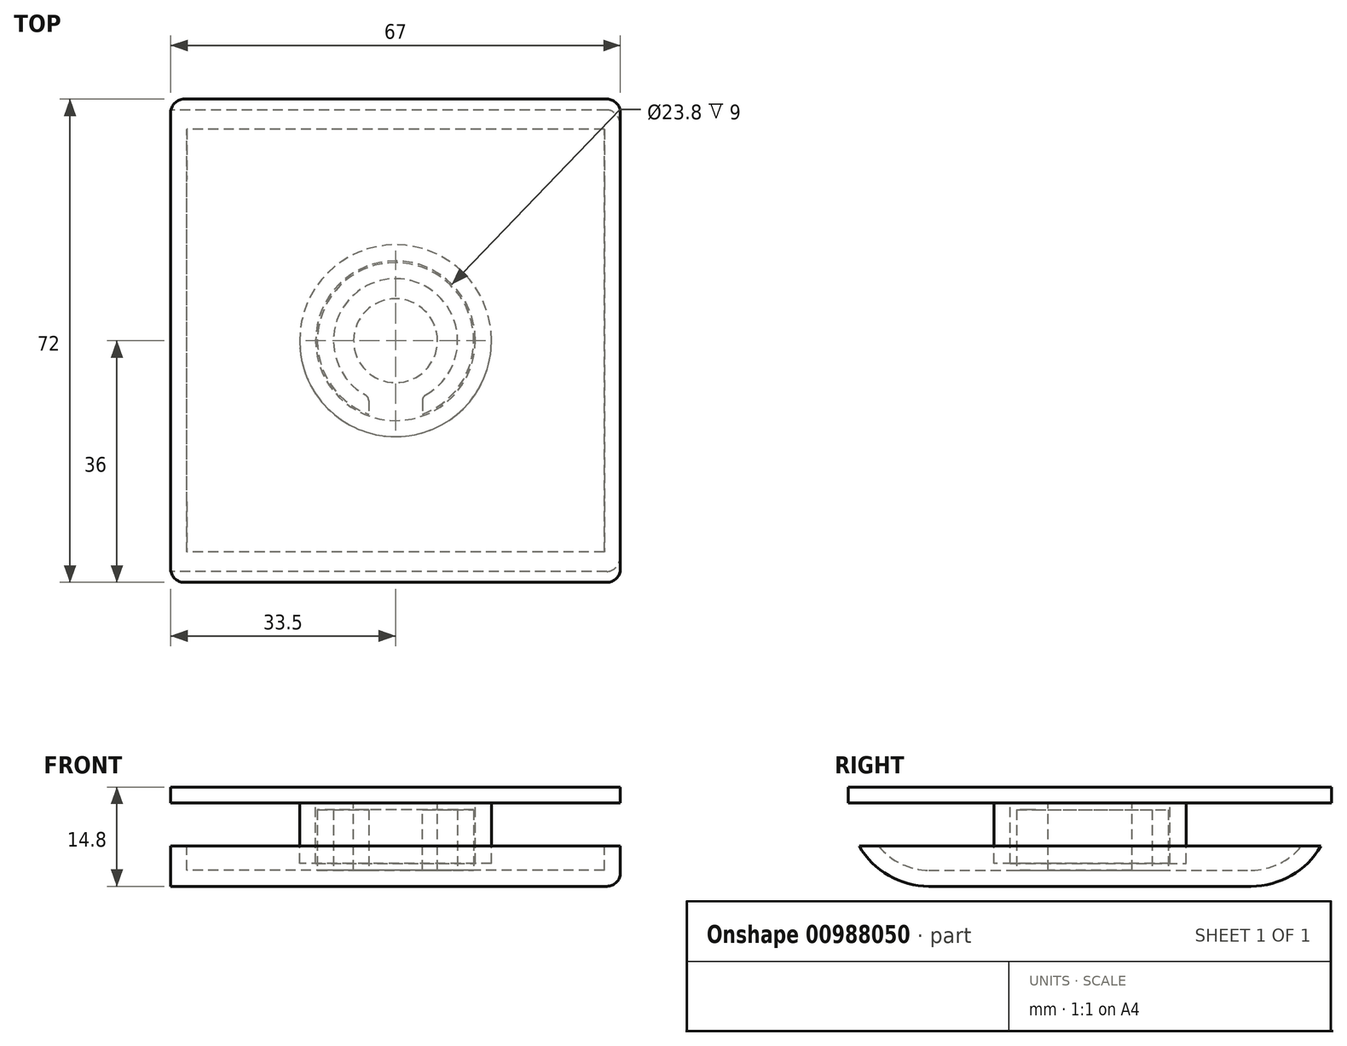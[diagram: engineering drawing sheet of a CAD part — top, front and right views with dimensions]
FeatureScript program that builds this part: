
annotation { "Feature Type Name" : "Feature", "Feature Type Description" : "" }
export const myFeature = defineFeature(function(context is Context, id is Id, definition is map)
    precondition{}
    {
        {
            var Q0;
            Q0=qCreatedBy(makeId("Top.planeOp"),FACE);
            var sketch = newSketch(context, id + "F0", { "sketchPlane" : qUnion([Q0])});
            skLineSegment(sketch, "E0.bottom", {"start": v(0, 0) * mm, "end": v(67, 0) * mm});
            skLineSegment(sketch, "E0.top", {"start": v(0, 72) * mm, "end": v(67, 72) * mm});
            skLineSegment(sketch, "E0.left", {"start": v(0, 0) * mm, "end": v(0, 72) * mm});
            skLineSegment(sketch, "E0.right", {"start": v(67, 0) * mm, "end": v(67, 72) * mm});
            skSolve(sketch);
        }
        {
            var Q0;
            Q0=makeQuery(id+"F0.imprint","IMPRINT",FACE,{"disambiguationData":[TD([[makeQuery(id+"F0.imprint","IMPRINT",EDGE,{"derivedFrom":sQuery(id+"F0.wireOp",EDGE,"E0.bottom")}),1.0]])]});
            extrude(context, id + "F1", {"entities" : qUnion([Q0]), "depth" : 6 * mm, "offsetDistance" : 25 * mm});
        }
        {
            var Q0;
            Q0=makeQuery(id+"F1.opExtrude","SWEPT_FACE",FACE,{"disambiguationData":[OSD([sQuery(id+"F0.wireOp",EDGE,"E0.left")])]});
            var sketch = newSketch(context, id + "F2", { "sketchPlane" : qUnion([Q0])});
            skLineSegment(sketch, "E1.0", {"start": v(-72, 12) * mm, "end": v(-72, 6) * mm});
            skLineSegment(sketch, "E2.0", {"start": v(-12, 0) * mm, "end": v(-60, 0) * mm});
            skLineSegment(sketch, "E3.0", {"start": v(0, 12) * mm, "end": v(0, 6) * mm});
            skLineSegment(sketch, "E4", {"start": v(-72, 6) * mm, "end": v(-72, 15.52) * mm});
            skLineSegment(sketch, "E5", {"start": v(0, 6) * mm, "end": v(0, 15.52) * mm});
            skPoint(sketch, "E6.visualSharp", {"position": v(-72, 0) * mm});
            skArc(sketch, "E6.filletArc", {"start": v(-72, 12) * mm, "mid": v(-68.49, 3.51) * mm, "end": v(-60, 0) * mm});
            skPoint(sketch, "E7.visualSharp", {"position": v(0, 0) * mm});
            skArc(sketch, "E7.filletArc", {"start": v(-12, 0) * mm, "mid": v(-3.51, 3.51) * mm, "end": v(0, 12) * mm});
            skLineSegment(sketch, "E8", {"start": v(-72, 6) * mm, "end": v(-72, 0) * mm});
            skLineSegment(sketch, "E9", {"start": v(-60, 0) * mm, "end": v(-12, 0) * mm});
            skLineSegment(sketch, "E10", {"start": v(0, 0) * mm, "end": v(0, 6) * mm});
            skSolve(sketch);
        }
        {
            var Q0;
            {var subQ6=sQuery(id+"F2.wireOp",EDGE,"E8");Q0=makeQuery(id+"F2.imprint","IMPRINT",FACE,{"disambiguationData":[TD([[makeQuery(id+"F2.imprint","IMPRINT",EDGE,{"derivedFrom":subQ6}),1.0]])]});}
            var Q1;
            {var subQ6=sQuery(id+"F2.wireOp",EDGE,"E10");Q1=makeQuery(id+"F2.imprint","IMPRINT",FACE,{"disambiguationData":[TD([[makeQuery(id+"F2.imprint","IMPRINT",EDGE,{"derivedFrom":subQ6}),-1.0]])]});}
            extrude(context, id + "F3", {"entities" : qUnion([Q0, Q1]), "operationType" : NewBodyOperationType.REMOVE, "endBound" : BoundingType.THROUGH_ALL, "oppositeDirection" : true, "depth" : 25 * mm, "offsetDistance" : 25 * mm});
        }
        {
            var Q0;
            Q0=makeQuery(id+"F3.boolean.opBoolean","COPY",EDGE,{"derivedFrom":makeQuery(id+"F3.opExtrude","CAP_EDGE",EDGE,{"disambiguationData":[OSD([sQuery(id+"F2.wireOp",EDGE,"E7.filletArc")])],"isStart":true})});
            var Q1;
            Q1=makeQuery(id+"F3.boolean.opBoolean","INTERSECT",EDGE,{"derivedFrom":[makeQuery(id+"F1.opExtrude","SWEPT_FACE",FACE,{"disambiguationData":[OSD([sQuery(id+"F0.wireOp",EDGE,"E0.right")])]}),makeQuery(id+"F3.opExtrude","SWEPT_FACE",FACE,{"disambiguationData":[OSD([sQuery(id+"F2.wireOp",EDGE,"E7.filletArc")])]})]});
            fillet(context, id + "F4", {"entities" : qUnion([Q0, Q1]), "radius" : 2 * mm, "tangentPropagation" : true, "allowEdgeOverflow" : false});
        }
        {
            var Q0;
            Q0=makeQuery(id+"F1.opExtrude","CAP_FACE",FACE,{"disambiguationData":[OSD([sQuery(id+"F0.wireOp",EDGE,"E0.bottom"),sQuery(id+"F0.wireOp",EDGE,"E0.top"),sQuery(id+"F0.wireOp",EDGE,"E0.left"),sQuery(id+"F0.wireOp",EDGE,"E0.right")])],"isStart":false});
            shell(context, id + "F5", {"entities" : qUnion([Q0]), "thickness" : 2.4 * mm});
        }
        {
            var Q0;
            Q0=makeQuery(id+"F5.opShell","OFFSET_FACE",FACE,{"disambiguationData":[OSD([sQuery(id+"F0.wireOp",EDGE,"E0.bottom"),sQuery(id+"F0.wireOp",EDGE,"E0.top"),sQuery(id+"F0.wireOp",EDGE,"E0.left"),sQuery(id+"F0.wireOp",EDGE,"E0.right")])]});
            var sketch = newSketch(context, id + "F6", { "sketchPlane" : qUnion([Q0])});
            skLineSegment(sketch, "E11.0", {"start": v(0, 4) * mm, "end": v(0, 68) * mm});
            skLineSegment(sketch, "E12.0", {"start": v(67, 4) * mm, "end": v(67, 68) * mm});
            skLineSegment(sketch, "E13.0", {"start": v(64.6, 60) * mm, "end": v(2.4, 60) * mm});
            skLineSegment(sketch, "E14.0", {"start": v(64.6, 12) * mm, "end": v(2.4, 12) * mm});
            skArc(sketch, "E15", {"start": v(37.5, 27.66) * mm, "mid": v(33.5, 45.25) * mm, "end": v(29.5, 27.66) * mm});
            skArc(sketch, "E16", {"start": v(37.5, 25.06) * mm, "mid": v(33.5, 47.65) * mm, "end": v(29.5, 25.06) * mm});
            skLineSegment(sketch, "E17", {"start": v(33.5, 36) * mm, "end": v(33.5, 24.35) * mm, "construction": true});
            skLineSegment(sketch, "E18", {"start": v(29.5, 27.66) * mm, "end": v(29.5, 25.06) * mm});
            skLineSegment(sketch, "E19", {"start": v(37.5, 27.66) * mm, "end": v(37.5, 25.06) * mm});
            skSolve(sketch);
        }
        {
            var Q0;
            Q0=makeQuery(id+"F6.imprint","IMPRINT",FACE,{"disambiguationData":[TD([[makeQuery(id+"F6.imprint","IMPRINT",EDGE,{"derivedFrom":sQuery(id+"F6.wireOp",EDGE,"E15")}),-1.0]])]});
            extrude(context, id + "F7", {"entities" : qUnion([Q0]), "operationType" : NewBodyOperationType.ADD, "depth" : 9 * mm, "offsetDistance" : 25 * mm});
        }
        {
            var Q0;
            Q0=makeQuery(id+"F7.opExtrude","SWEPT_EDGE",EDGE,{"disambiguationData":[OSD([sQuery(id+"F6.wireOp",EDGE,"E15"),sQuery(id+"F6.wireOp",EDGE,"E18")])]});
            var Q1;
            Q1=makeQuery(id+"F7.opExtrude","SWEPT_EDGE",EDGE,{"disambiguationData":[OSD([sQuery(id+"F6.wireOp",EDGE,"E15"),sQuery(id+"F6.wireOp",EDGE,"E19")])]});
            fillet(context, id + "F8", {"entities" : qUnion([Q0, Q1]), "radius" : 1 * mm, "tangentPropagation" : true, "allowEdgeOverflow" : false});
        }
        {
            var Q0;
            Q0=qCreatedBy(makeId("Top.planeOp"),FACE);
            cPlane(context, id + "F9", {"entities" : qUnion([Q0]), "cplaneType" : CPlaneType.OFFSET, "offset" : (11.4 + 2.4 + 1) * mm, "width" : 150 * mm, "height" : 150 * mm});
        }
        {
            var Q0;
            Q0=qCreatedBy(id+"F9.planeOp",FACE);
            var sketch = newSketch(context, id + "F10", { "sketchPlane" : qUnion([Q0])});
            skLineSegment(sketch, "E20.bottom", {"start": v(0, 0) * mm, "end": v(67, 0) * mm});
            skLineSegment(sketch, "E20.top", {"start": v(0, 72) * mm, "end": v(67, 72) * mm});
            skLineSegment(sketch, "E20.left", {"start": v(0, 0) * mm, "end": v(0, 72) * mm});
            skLineSegment(sketch, "E20.right", {"start": v(67, 0) * mm, "end": v(67, 72) * mm});
            skSolve(sketch);
        }
        {
            var Q0;
            Q0 = qSketchRegion(id + "F10", true);
            extrude(context, id + "F11", {"entities" : qUnion([Q0]), "oppositeDirection" : true, "depth" : 2.4 * mm, "offsetDistance" : 25 * mm});
        }
        {
            var Q0;
            Q0=makeQuery(id+"F11.opExtrude","CAP_FACE",FACE,{"disambiguationData":[OSD([sQuery(id+"F10.wireOp",EDGE,"E20.bottom"),sQuery(id+"F10.wireOp",EDGE,"E20.top"),sQuery(id+"F10.wireOp",EDGE,"E20.left"),sQuery(id+"F10.wireOp",EDGE,"E20.right")])],"isStart":false});
            var sketch = newSketch(context, id + "F12", { "sketchPlane" : qUnion([Q0])});
            skCircle(sketch, "E21", {"center": v(33.5, -36) * mm, "radius": 11.9 * mm});
            skPoint(sketch, "E21.centerSnap0", {"position": v(67, -36) * mm});
            skCircle(sketch, "E22", {"center": v(33.5, -36) * mm, "radius": 6.25 * mm});
            skCircle(sketch, "E23", {"center": v(33.5, -36) * mm, "radius": 14.3 * mm});
            skSolve(sketch);
        }
        {
            var Q0;
            Q0=makeQuery(id+"F12.imprint","IMPRINT",FACE,{"disambiguationData":[TD([[makeQuery(id+"F12.imprint","IMPRINT",EDGE,{"derivedFrom":sQuery(id+"F12.wireOp",EDGE,"E22")}),1.0]])]});
            extrude(context, id + "F13", {"entities" : qUnion([Q0]), "operationType" : NewBodyOperationType.ADD, "depth" : 10 * mm, "offsetDistance" : 25 * mm});
        }
        {
            var Q0;
            Q0=makeQuery(id+"F12.imprint","IMPRINT",FACE,{"disambiguationData":[TD([[makeQuery(id+"F12.imprint","IMPRINT",EDGE,{"derivedFrom":sQuery(id+"F12.wireOp",EDGE,"E21")}),-1.0]])]});
            var Q1;
            Q1=sQuery(id+"F12.wireOp",EDGE,"E23");
            var Q2;
            Q2=sQuery(id+"F12.wireOp",EDGE,"E21");
            extrude(context, id + "F14", {"entities" : qUnion([Q0]), "operationType" : NewBodyOperationType.ADD, "surfaceEntities" : qUnion([Q1, Q2]), "depth" : 9 * mm, "offsetDistance" : 25 * mm});
        }
        {
            var Q0;
            Q0=makeQuery(id+"F11.opExtrude","SWEPT_EDGE",EDGE,{"disambiguationData":[OSD([sQuery(id+"F10.wireOp",EDGE,"E20.bottom"),sQuery(id+"F10.wireOp",EDGE,"E20.right")])]});
            var Q1;
            Q1=makeQuery(id+"F11.opExtrude","SWEPT_EDGE",EDGE,{"disambiguationData":[OSD([sQuery(id+"F10.wireOp",EDGE,"E20.bottom"),sQuery(id+"F10.wireOp",EDGE,"E20.left")])]});
            var Q2;
            Q2=makeQuery(id+"F11.opExtrude","SWEPT_EDGE",EDGE,{"disambiguationData":[OSD([sQuery(id+"F10.wireOp",EDGE,"E20.top"),sQuery(id+"F10.wireOp",EDGE,"E20.left")])]});
            var Q3;
            Q3=makeQuery(id+"F11.opExtrude","SWEPT_EDGE",EDGE,{"disambiguationData":[OSD([sQuery(id+"F10.wireOp",EDGE,"E20.top"),sQuery(id+"F10.wireOp",EDGE,"E20.right")])]});
            fillet(context, id + "F15", {"entities" : qUnion([Q0, Q1, Q2, Q3]), "radius" : 2 * mm, "tangentPropagation" : true, "allowEdgeOverflow" : false});
        }
    });
